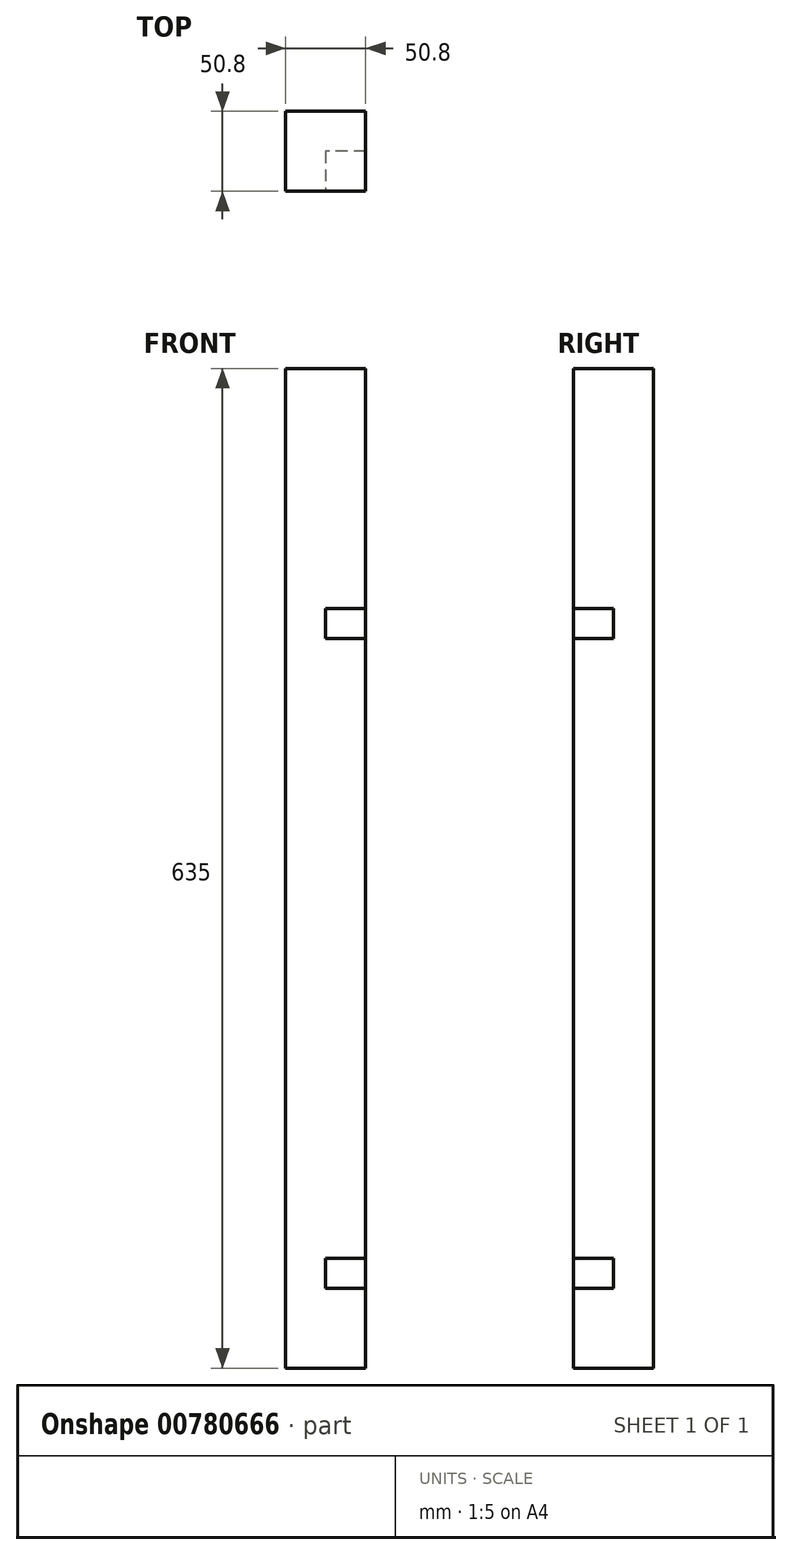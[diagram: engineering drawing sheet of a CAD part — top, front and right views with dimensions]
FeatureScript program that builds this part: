
annotation { "Feature Type Name" : "Feature", "Feature Type Description" : "" }
export const myFeature = defineFeature(function(context is Context, id is Id, definition is map)
    precondition{}
    {
        {
            var Q0;
            Q0=qCreatedBy(makeId("Top.planeOp"),FACE);
            var sketch = newSketch(context, id + "F0", { "sketchPlane" : qUnion([Q0])});
            skLineSegment(sketch, "E0.bottom", {"start": v(0, 0) * mm, "end": v(50.8, 0) * mm});
            skLineSegment(sketch, "E0.top", {"start": v(0, 50.8) * mm, "end": v(50.8, 50.8) * mm});
            skLineSegment(sketch, "E0.left", {"start": v(0, 0) * mm, "end": v(0, 50.8) * mm});
            skLineSegment(sketch, "E0.right", {"start": v(50.8, 0) * mm, "end": v(50.8, 50.8) * mm});
            skSolve(sketch);
        }
        {
            var Q0;
            Q0=makeQuery(id+"F0.imprint","IMPRINT",FACE,{"disambiguationData":[TD([[makeQuery(id+"F0.imprint","IMPRINT",EDGE,{"derivedFrom":sQuery(id+"F0.wireOp",EDGE,"E0.bottom")}),1.0]])]});
            extrude(context, id + "F1", {"entities" : qUnion([Q0]), "depth" : 635 * mm, "offsetDistance" : 25.4 * mm});
        }
        {
            var Q0;
            Q0=makeQuery(id+"F1.opExtrude","SWEPT_FACE",FACE,{"disambiguationData":[OSD([sQuery(id+"F0.wireOp",EDGE,"E0.bottom")])]});
            var sketch = newSketch(context, id + "F2", { "sketchPlane" : qUnion([Q0])});
            skLineSegment(sketch, "E1.bottom", {"start": v(50.8, 50.8) * mm, "end": v(25.4, 50.8) * mm});
            skLineSegment(sketch, "E1.top", {"start": v(50.8, 69.85) * mm, "end": v(25.4, 69.85) * mm});
            skLineSegment(sketch, "E1.left", {"start": v(50.8, 50.8) * mm, "end": v(50.8, 69.85) * mm});
            skLineSegment(sketch, "E1.right", {"start": v(25.4, 50.8) * mm, "end": v(25.4, 69.85) * mm});
            skLineSegment(sketch, "E2.bottom", {"start": v(50.8, 463.55) * mm, "end": v(25.4, 463.55) * mm});
            skLineSegment(sketch, "E2.top", {"start": v(50.8, 482.6) * mm, "end": v(25.4, 482.6) * mm});
            skLineSegment(sketch, "E2.left", {"start": v(50.8, 463.55) * mm, "end": v(50.8, 482.6) * mm});
            skLineSegment(sketch, "E2.right", {"start": v(25.4, 463.55) * mm, "end": v(25.4, 482.6) * mm});
            skSolve(sketch);
        }
        {
            var Q0;
            Q0=makeQuery(id+"F2.imprint","IMPRINT",FACE,{"disambiguationData":[TD([[makeQuery(id+"F2.imprint","IMPRINT",EDGE,{"derivedFrom":sQuery(id+"F2.wireOp",EDGE,"E1.bottom")}),-1.0]])]});
            var Q1;
            Q1=makeQuery(id+"F2.imprint","IMPRINT",FACE,{"disambiguationData":[TD([[makeQuery(id+"F2.imprint","IMPRINT",EDGE,{"derivedFrom":sQuery(id+"F2.wireOp",EDGE,"E2.bottom")}),-1.0]])]});
            extrude(context, id + "F3", {"entities" : qUnion([Q0, Q1]), "operationType" : NewBodyOperationType.REMOVE, "oppositeDirection" : true, "depth" : 25.4 * mm, "offsetDistance" : 25.4 * mm});
        }
    });
